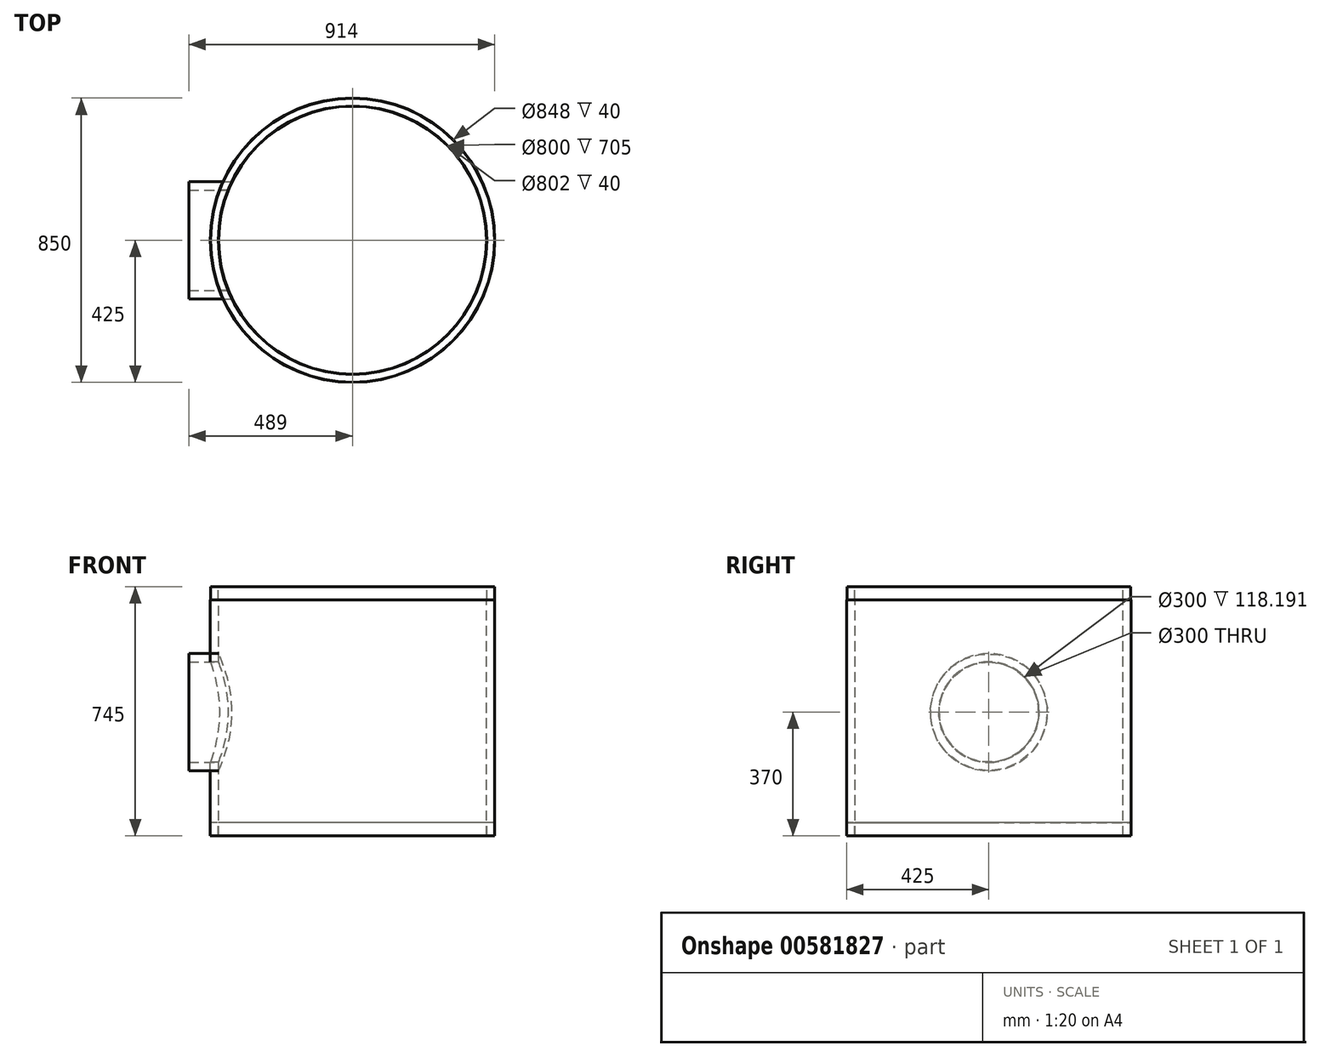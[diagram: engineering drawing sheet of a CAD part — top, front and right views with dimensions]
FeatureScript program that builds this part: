
annotation { "Feature Type Name" : "Feature", "Feature Type Description" : "" }
export const myFeature = defineFeature(function(context is Context, id is Id, definition is map)
    precondition{}
    {
        {
            var Q0;
            Q0=qCreatedBy(makeId("Front.planeOp"),FACE);
            var sketch = newSketch(context, id + "F0", { "sketchPlane" : qUnion([Q0])});
            skLineSegment(sketch, "E0", {"start": v(0, 722.18) * mm, "end": v(0, -793.11) * mm, "construction": true});
            skLineSegment(sketch, "E1", {"start": v(-400, -370) * mm, "end": v(-400, 335) * mm});
            skLineSegment(sketch, "E2", {"start": v(-400, 335) * mm, "end": v(-401, 335) * mm});
            skLineSegment(sketch, "E3", {"start": v(-401, 335) * mm, "end": v(-401, 375) * mm});
            skLineSegment(sketch, "E4", {"start": v(-401, 375) * mm, "end": v(-424, 375) * mm});
            skLineSegment(sketch, "E5", {"start": v(-424, 375) * mm, "end": v(-424, 335) * mm});
            skLineSegment(sketch, "E6", {"start": v(-424, 335) * mm, "end": v(-425, 335) * mm});
            skLineSegment(sketch, "E7", {"start": v(-425, 335) * mm, "end": v(-425, -370) * mm});
            skLineSegment(sketch, "E8", {"start": v(-425, -370) * mm, "end": v(-424, -370) * mm});
            skLineSegment(sketch, "E9", {"start": v(-424, -370) * mm, "end": v(-424, -330) * mm});
            skLineSegment(sketch, "E10", {"start": v(-424, -330) * mm, "end": v(-401, -330) * mm});
            skLineSegment(sketch, "E11", {"start": v(-401, -330) * mm, "end": v(-401, -370) * mm});
            skLineSegment(sketch, "E12", {"start": v(-401, -370) * mm, "end": v(-400, -370) * mm});
            skLineSegment(sketch, "E13", {"start": v(0, 0) * mm, "end": v(-928, 0) * mm, "construction": true});
            skLineSegment(sketch, "E14", {"start": v(0, -150) * mm, "end": v(-489, -150) * mm});
            skLineSegment(sketch, "E15", {"start": v(-489, -150) * mm, "end": v(-489, -175) * mm});
            skLineSegment(sketch, "E16", {"start": v(-489, -175) * mm, "end": v(0, -175) * mm});
            skLineSegment(sketch, "E17", {"start": v(0, -175) * mm, "end": v(0, -150) * mm});
            skLineSegment(sketch, "E18", {"start": v(-489, -150) * mm, "end": v(-489, 0) * mm});
            skLineSegment(sketch, "E19", {"start": v(-489, 0) * mm, "end": v(-464, 0) * mm});
            skLineSegment(sketch, "E20", {"start": v(-464, 0) * mm, "end": v(-464, -150) * mm});
            skSolve(sketch);
        }
        {
            var Q0;
            {var subQ0=sQuery(id+"F0.wireOp",EDGE,"E2");Q0=makeQuery(id+"F0.imprint","IMPRINT",FACE,{"disambiguationData":[TD([[makeQuery(id+"F0.imprint","IMPRINT",EDGE,{"derivedFrom":subQ0}),1.0]])]});}
            var Q1;
            {var subQ0=sQuery(id+"F0.wireOp",EDGE,"E16");var subQ1=sQuery(id+"F0.wireOp",EDGE,"E1");var subQ2=makeQuery(id+"F0.imprint","INTERSECT",VERTEX,{"derivedFrom":[subQ1,subQ0]});Q1=makeQuery(id+"F0.imprint","IMPRINT",FACE,{"disambiguationData":[TD([[makeQuery(id+"F0.imprint","IMPRINT",EDGE,{"disambiguationData":[TD([[subQ2,-1.0]])],"derivedFrom":subQ1}),1.0]])]});}
            var Q2;
            {var subQ0=sQuery(id+"F0.wireOp",EDGE,"E8");Q2=makeQuery(id+"F0.imprint","IMPRINT",FACE,{"disambiguationData":[TD([[makeQuery(id+"F0.imprint","IMPRINT",EDGE,{"derivedFrom":subQ0}),1.0]])]});}
            var Q3;
            Q3=sQuery(id+"F0.wireOp",EDGE,"E0");
            revolve(context, id + "F1", {"entities" : qUnion([Q0, Q1, Q2]), "axis" : qUnion([Q3]), "revolveType" : RevolveType.FULL});
        }
        {
            var Q0;
            {var subQ0=sQuery(id+"F0.wireOp",EDGE,"E18");Q0=makeQuery(id+"F0.imprint","IMPRINT",FACE,{"disambiguationData":[TD([[makeQuery(id+"F0.imprint","IMPRINT",EDGE,{"derivedFrom":subQ0}),-1.0]])]});}
            var Q1;
            {var subQ0=sQuery(id+"F0.wireOp",EDGE,"E15");Q1=makeQuery(id+"F0.imprint","IMPRINT",FACE,{"disambiguationData":[TD([[makeQuery(id+"F0.imprint","IMPRINT",EDGE,{"derivedFrom":subQ0}),1.0]])]});}
            var Q2;
            {var subQ0=sQuery(id+"F0.wireOp",EDGE,"E16");var subQ1=sQuery(id+"F0.wireOp",EDGE,"E1");var subQ2=makeQuery(id+"F0.imprint","INTERSECT",VERTEX,{"derivedFrom":[subQ1,subQ0]});Q2=makeQuery(id+"F0.imprint","IMPRINT",FACE,{"disambiguationData":[TD([[makeQuery(id+"F0.imprint","IMPRINT",EDGE,{"disambiguationData":[TD([[subQ2,-1.0]])],"derivedFrom":subQ1}),1.0]])]});}
            var Q3;
            {var subQ5=sQuery(id+"F0.wireOp",EDGE,"E17");Q3=makeQuery(id+"F0.imprint","IMPRINT",FACE,{"disambiguationData":[TD([[makeQuery(id+"F0.imprint","IMPRINT",EDGE,{"derivedFrom":subQ5}),1.0]])]});}
            var Q4;
            Q4=sQuery(id+"F0.wireOp",EDGE,"E13");
            revolve(context, id + "F2", {"entities" : qUnion([Q0, Q1, Q2, Q3]), "axis" : qUnion([Q4]), "revolveType" : RevolveType.FULL});
        }
        {
            var Q0;
            Q0=makeQuery(id+"F2.opRevolve","SWEPT_FACE",FACE,{"disambiguationData":[OSD([sQuery(id+"F0.wireOp",EDGE,"E15"),sQuery(id+"F0.wireOp",EDGE,"E18")])]});
            var sketch = newSketch(context, id + "F3", { "sketchPlane" : qUnion([Q0])});
            skCircle(sketch, "E21", {"center": v(0, 0) * mm, "radius": 150 * mm});
            skSolve(sketch);
        }
        {
            var Q0;
            Q0=qSketchRegion(id+"F3",true);
            extrude(context, id + "F4", {"entities" : qUnion([Q0]), "operationType" : NewBodyOperationType.REMOVE, "oppositeDirection" : true, "offsetDistance" : 25 * mm, "depth" : 600 * mm});
        }
        {
            var Q0;
            Q0=makeQuery(id+"F1.opRevolve","SWEPT_FACE",FACE,{"disambiguationData":[OSD([sQuery(id+"F0.wireOp",EDGE,"E4")])]});
            var sketch = newSketch(context, id + "F5", { "sketchPlane" : qUnion([Q0])});
            skCircle(sketch, "E22", {"center": v(0, 0) * mm, "radius": 400 * mm});
            skSolve(sketch);
        }
        {
            var Q0;
            Q0=qSketchRegion(id+"F5",true);
            extrude(context, id + "F6", {"entities" : qUnion([Q0]), "operationType" : NewBodyOperationType.REMOVE, "oppositeDirection" : true, "depth" : 1200 * mm});
        }
    });
